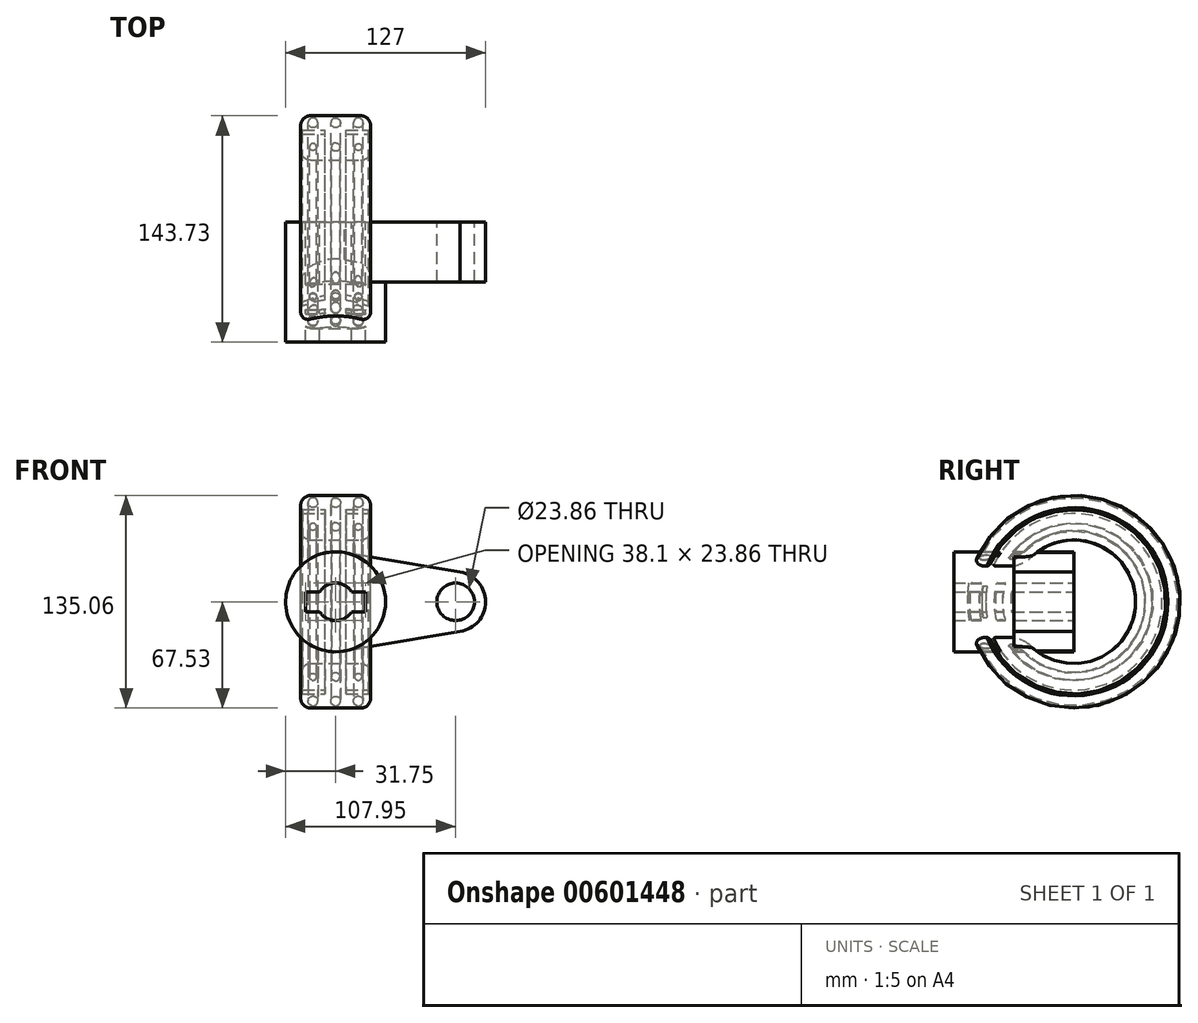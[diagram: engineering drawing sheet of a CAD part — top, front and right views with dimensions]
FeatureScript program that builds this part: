
annotation { "Feature Type Name" : "Feature", "Feature Type Description" : "" }
export const myFeature = defineFeature(function(context is Context, id is Id, definition is map)
    precondition{}
    {
        {
            var Q0;
            Q0=qCreatedBy(makeId("Front.planeOp"),FACE);
            var sketch = newSketch(context, id + "F0", { "sketchPlane" : qUnion([Q0])});
            skCircle(sketch, "E0", {"center": v(0, 0) * mm, "radius": 31.75 * mm});
            skCircle(sketch, "E1", {"center": v(76.2, 0) * mm, "radius": 19.05 * mm});
            skLineSegment(sketch, "E2", {"start": v(5.3, 31.3) * mm, "end": v(79.38, 18.78) * mm});
            skLineSegment(sketch, "E3", {"start": v(5.3, -31.3) * mm, "end": v(79.38, -18.78) * mm});
            skCircle(sketch, "E4", {"center": v(0, 0) * mm, "radius": 11.93 * mm});
            skCircle(sketch, "E5", {"center": v(76.2, 0) * mm, "radius": 11.93 * mm});
            skLineSegment(sketch, "E6.bottom", {"start": v(19.05, 6.35) * mm, "end": v(-19.05, 6.35) * mm});
            skLineSegment(sketch, "E6.top", {"start": v(19.05, -6.35) * mm, "end": v(-19.05, -6.35) * mm});
            skLineSegment(sketch, "E6.left", {"start": v(19.05, 6.35) * mm, "end": v(19.05, -6.35) * mm});
            skLineSegment(sketch, "E6.right", {"start": v(-19.05, 6.35) * mm, "end": v(-19.05, -6.35) * mm});
            skSolve(sketch);
        }
        {
            var Q0;
            Q0=makeQuery(id+"F0.imprint","IMPRINT",FACE,{"disambiguationData":[TD([[makeQuery(id+"F0.imprint","IMPRINT",EDGE,{"derivedFrom":sQuery(id+"F0.wireOp",EDGE,"E5")}),-1.0]])]});
            var Q1;
            {var subQ0=sQuery(id+"F0.wireOp",EDGE,"E2");Q1=makeQuery(id+"F0.imprint","IMPRINT",FACE,{"disambiguationData":[TD([[makeQuery(id+"F0.imprint","IMPRINT",EDGE,{"derivedFrom":subQ0}),-1.0]])]});}
            var Q2;
            {var subQ7=sQuery(id+"F0.wireOp",EDGE,"E6.left");Q2=makeQuery(id+"F0.imprint","IMPRINT",FACE,{"disambiguationData":[TD([[makeQuery(id+"F0.imprint","IMPRINT",EDGE,{"derivedFrom":subQ7}),1.0]])]});}
            extrude(context, id + "F1", {"entities" : qUnion([Q0, Q1, Q2]), "depth" : 38.1 * mm, "offsetDistance" : 25.4 * mm});
        }
        {
            var Q0;
            {var subQ7=sQuery(id+"F0.wireOp",EDGE,"E6.left");Q0=makeQuery(id+"F0.imprint","IMPRINT",FACE,{"disambiguationData":[TD([[makeQuery(id+"F0.imprint","IMPRINT",EDGE,{"derivedFrom":subQ7}),1.0]])]});}
            extrude(context, id + "F2", {"entities" : qUnion([Q0]), "operationType" : NewBodyOperationType.ADD, "depth" : 76.2 * mm, "offsetDistance" : 25.4 * mm});
        }
        {
            var Q0;
            Q0=qCreatedBy(makeId("Front.planeOp"),FACE);
            var sketch = newSketch(context, id + "F3", { "sketchPlane" : qUnion([Q0])});
            skLineSegment(sketch, "E7", {"start": v(0, 67.53) * mm, "end": v(-15.86, 67.53) * mm});
            skLineSegment(sketch, "E8", {"start": v(-22.2, 61.18) * mm, "end": v(-22.2, 59.77) * mm});
            skLineSegment(sketch, "E9", {"start": v(-20.94, 58.5) * mm, "end": v(-6.59, 58.5) * mm});
            skLineSegment(sketch, "E10", {"start": v(-6.59, 58.5) * mm, "end": v(-6.59, 55.99) * mm});
            skLineSegment(sketch, "E11", {"start": v(-6.59, 55.99) * mm, "end": v(-20.94, 55.99) * mm});
            skLineSegment(sketch, "E12", {"start": v(-22.2, 54.72) * mm, "end": v(-22.2, 45.6) * mm});
            skLineSegment(sketch, "E13", {"start": v(-15.86, 39.25) * mm, "end": v(0, 39.25) * mm});
            skCircle(sketch, "E14", {"center": v(-14.4, 63.01) * mm, "radius": 3.1 * mm});
            skCircle(sketch, "E15", {"center": v(0, 63.01) * mm, "radius": 3.05 * mm});
            skCircle(sketch, "E16", {"center": v(0, 47.62) * mm, "radius": 2.7 * mm});
            skCircle(sketch, "E17", {"center": v(-14.4, 47.62) * mm, "radius": 2.23 * mm});
            skPoint(sketch, "E18.visualSharp", {"position": v(-22.2, 67.53) * mm});
            skArc(sketch, "E18.filletArc", {"start": v(-15.86, 67.53) * mm, "mid": v(-20.35, 65.67) * mm, "end": v(-22.2, 61.18) * mm});
            skPoint(sketch, "E19.visualSharp", {"position": v(-22.2, 39.25) * mm});
            skArc(sketch, "E19.filletArc", {"start": v(-22.2, 45.6) * mm, "mid": v(-20.35, 41.1) * mm, "end": v(-15.86, 39.25) * mm});
            skPoint(sketch, "E20.visualSharp", {"position": v(-22.2, 58.5) * mm});
            skArc(sketch, "E20.filletArc", {"start": v(-22.2, 59.77) * mm, "mid": v(-21.84, 58.87) * mm, "end": v(-20.94, 58.5) * mm});
            skPoint(sketch, "E21.visualSharp", {"position": v(-22.2, 55.99) * mm});
            skArc(sketch, "E21.filletArc", {"start": v(-20.94, 55.99) * mm, "mid": v(-21.84, 55.61) * mm, "end": v(-22.2, 54.72) * mm});
            skArc(sketch, "E22.MirrorCS", {"start": v(20.94, 55.99) * mm, "mid": v(21.84, 55.61) * mm, "end": v(22.2, 54.72) * mm});
            skLineSegment(sketch, "E23.MirrorCS", {"start": v(22.2, 61.18) * mm, "end": v(22.2, 59.77) * mm});
            skArc(sketch, "E24.MirrorCS", {"start": v(22.2, 59.77) * mm, "mid": v(21.84, 58.87) * mm, "end": v(20.94, 58.5) * mm});
            skLineSegment(sketch, "E25.MirrorCS", {"start": v(6.59, 58.5) * mm, "end": v(6.59, 55.99) * mm});
            skCircle(sketch, "E26.MirrorC", {"center": v(14.4, 63.01) * mm, "radius": 3.1 * mm});
            skPoint(sketch, "E27.MirrorP", {"position": v(22.2, 58.5) * mm});
            skPoint(sketch, "E28.MirrorP", {"position": v(22.2, 55.99) * mm});
            skPoint(sketch, "E29.MirrorP", {"position": v(22.2, 39.25) * mm});
            skLineSegment(sketch, "E30.MirrorCS", {"start": v(15.86, 39.25) * mm, "end": v(0, 39.25) * mm});
            skPoint(sketch, "E31.MirrorP", {"position": v(22.2, 67.53) * mm});
            skLineSegment(sketch, "E32.MirrorCS", {"start": v(0, 67.53) * mm, "end": v(15.86, 67.53) * mm});
            skArc(sketch, "E33.MirrorCS", {"start": v(22.2, 45.6) * mm, "mid": v(20.35, 41.1) * mm, "end": v(15.86, 39.25) * mm});
            skLineSegment(sketch, "E34.MirrorCS", {"start": v(6.59, 55.99) * mm, "end": v(20.94, 55.99) * mm});
            skCircle(sketch, "E35.MirrorC", {"center": v(14.4, 47.62) * mm, "radius": 2.23 * mm});
            skLineSegment(sketch, "E36.MirrorCS", {"start": v(20.94, 58.5) * mm, "end": v(6.59, 58.5) * mm});
            skArc(sketch, "E37.MirrorCS", {"start": v(15.86, 67.53) * mm, "mid": v(20.35, 65.67) * mm, "end": v(22.2, 61.18) * mm});
            skLineSegment(sketch, "E38.MirrorCS", {"start": v(22.2, 54.72) * mm, "end": v(22.2, 45.6) * mm});
            skLineSegment(sketch, "E39", {"start": v(75.88, 0) * mm, "end": v(-74.85, 0) * mm, "construction": true});
            skSolve(sketch);
        }
        {
            var Q0;
            Q0=makeQuery(id+"F3.imprint","IMPRINT",FACE,{"disambiguationData":[TD([[makeQuery(id+"F3.imprint","IMPRINT",EDGE,{"derivedFrom":sQuery(id+"F3.wireOp",EDGE,"E7")}),1.0]])]});
            var Q1;
            Q1=sQuery(id+"F3.wireOp",EDGE,"E39");
            revolve(context, id + "F4", {"operationType" : NewBodyOperationType.ADD, "entities" : qUnion([Q0]), "axis" : qUnion([Q1]), "revolveType" : RevolveType.FULL});
        }
    });
